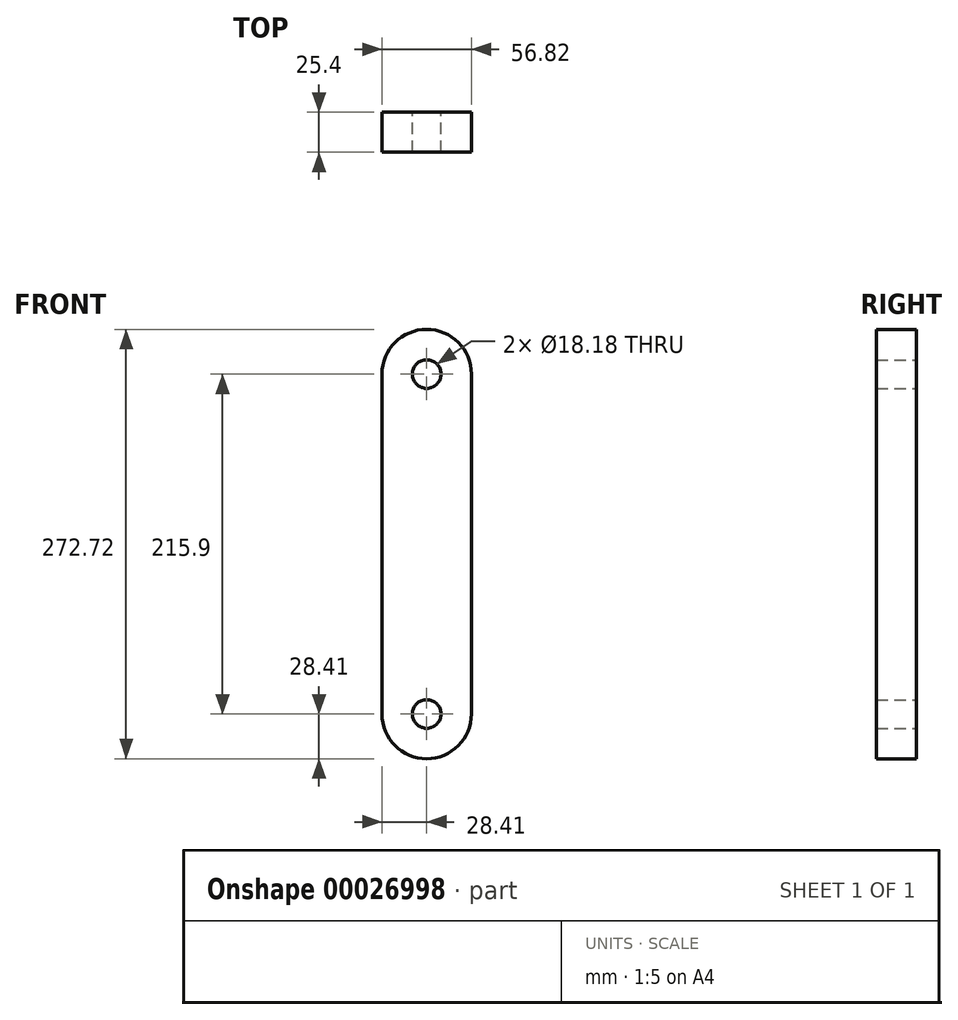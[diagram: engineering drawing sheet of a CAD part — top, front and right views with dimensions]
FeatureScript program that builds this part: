
annotation { "Feature Type Name" : "Feature", "Feature Type Description" : "" }
export const myFeature = defineFeature(function(context is Context, id is Id, definition is map)
    precondition{}
    {
        {
            var Q0;
            Q0=qCreatedBy(makeId("Front.planeOp"),FACE);
            var sketch = newSketch(context, id + "F0", { "sketchPlane" : qUnion([Q0])});
            skCircle(sketch, "E0", {"center": v(31.75, -44.45) * mm, "radius": 28.4 * mm});
            skCircle(sketch, "E1", {"center": v(31.75, -260.35) * mm, "radius": 28.4 * mm});
            skLineSegment(sketch, "E2", {"start": v(3.34, -44.45) * mm, "end": v(3.34, -260.35) * mm});
            skLineSegment(sketch, "E3", {"start": v(60.16, -44.45) * mm, "end": v(60.16, -260.35) * mm});
            skCircle(sketch, "E4", {"center": v(31.75, -260.35) * mm, "radius": 9.1 * mm});
            skCircle(sketch, "E5", {"center": v(31.75, -44.45) * mm, "radius": 9.1 * mm});
            skSolve(sketch);
        }
        {
            var Q0;
            Q0=makeQuery(id+"F0.imprint","IMPRINT",FACE,{"disambiguationData":[TD([[makeQuery(id+"F0.imprint","IMPRINT",EDGE,{"derivedFrom":sQuery(id+"F0.wireOp",EDGE,"E5")}),-1.0]])]});
            var Q1;
            {var subQ1=sQuery(id+"F0.wireOp",EDGE,"E2");Q1=makeQuery(id+"F0.imprint","IMPRINT",FACE,{"disambiguationData":[TD([[makeQuery(id+"F0.imprint","IMPRINT",EDGE,{"derivedFrom":subQ1}),1.0]])]});}
            var Q2;
            Q2=makeQuery(id+"F0.imprint","IMPRINT",FACE,{"disambiguationData":[TD([[makeQuery(id+"F0.imprint","IMPRINT",EDGE,{"derivedFrom":sQuery(id+"F0.wireOp",EDGE,"E4")}),-1.0]])]});
            extrude(context, id + "F1", {"entities" : qUnion([Q0, Q1, Q2]), "endBound" : BoundingType.SYMMETRIC, "depth" : 25.4 * mm});
        }
    });
